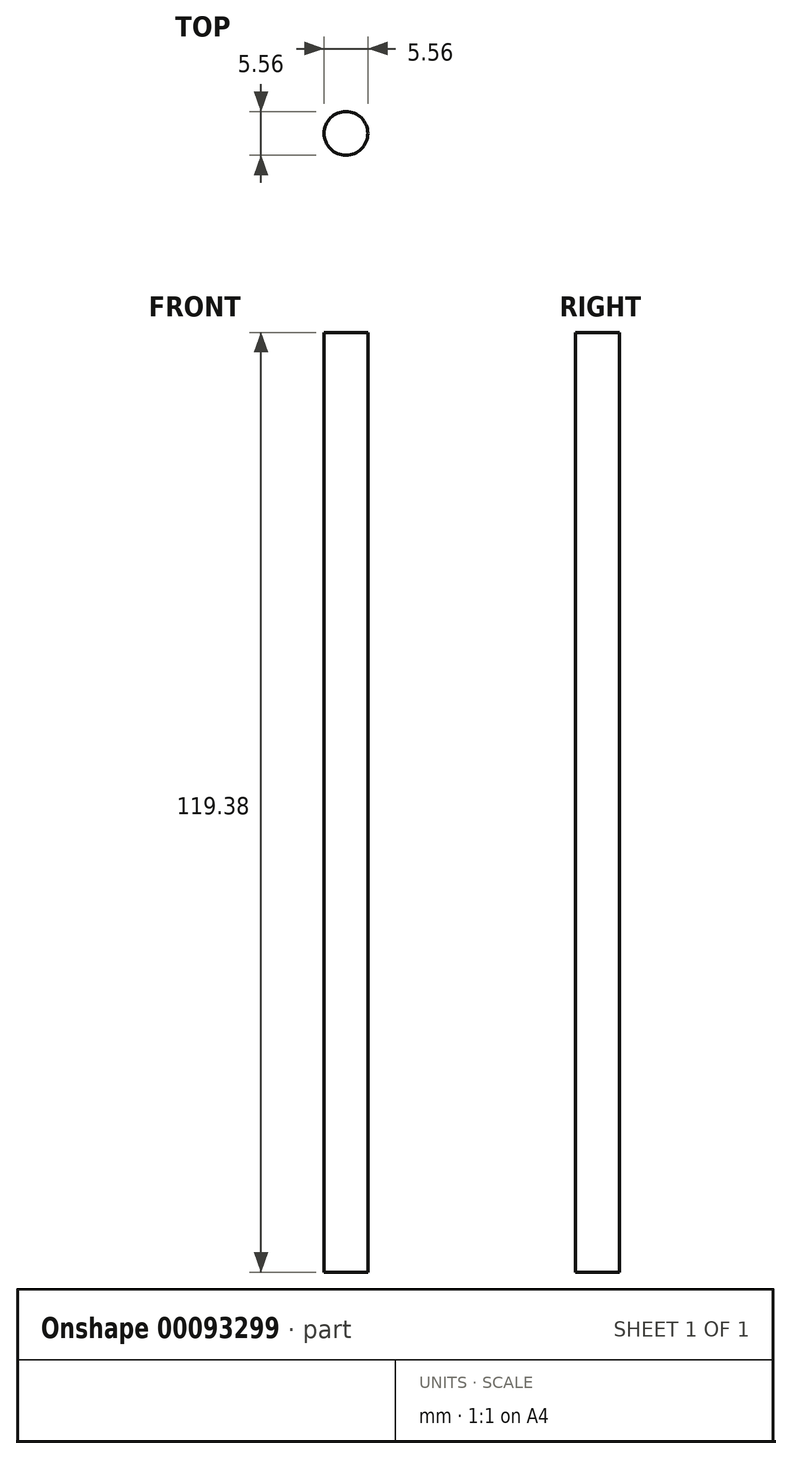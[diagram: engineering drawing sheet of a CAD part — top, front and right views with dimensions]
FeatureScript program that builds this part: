
annotation { "Feature Type Name" : "Feature", "Feature Type Description" : "" }
export const myFeature = defineFeature(function(context is Context, id is Id, definition is map)
    precondition{}
    {
        {
            var Q0;
            Q0=qCreatedBy(makeId("Top.planeOp"),FACE);
            var sketch = newSketch(context, id + "F0", { "sketchPlane" : qUnion([Q0])});
            skCircle(sketch, "E0", {"center": v(0, 0) * mm, "radius": 2.78 * mm});
            skSolve(sketch);
        }
        {
            var Q0;
            Q0 = qSketchRegion(id + "F0", true);
            extrude(context, id + "F1", {"entities" : qUnion([Q0]), "depth" : 119.38 * mm});
        }
    });
